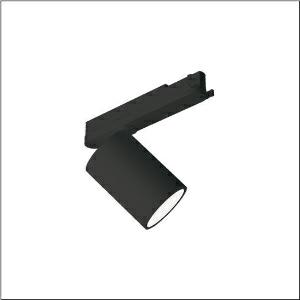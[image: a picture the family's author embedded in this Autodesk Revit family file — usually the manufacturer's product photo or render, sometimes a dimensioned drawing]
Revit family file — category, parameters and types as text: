
# Revit family: spot_31_51sf34mad4b
name_source: partatom
category: Lighting Fixtures
units: mm (PartAtom-declared; Revit-internal decimal feet)

## family parameters
Cut with Voids When Loaded = No
Host = Face
Light Source = No
Part Type = Normal
Room Calculation Point = No
Round Connector Dimension = Use Diameter
Shared = No

## types (1)
- --- (1 x LED, 5250 lm, 41.4 W, 4000K)
    Apparent Load = 41 VA
    CIE Flux Codes = 93 97 100 100 100
    Color Rendering = 90
    Color Temperature = 4000K
    Default Elevation = 1800 mm
    Description = Spot 31, directional spotlight, light control with lens, of PMMA, LED rated luminous flux: 5.040lm, light colour: 940, with 3-phase adapter, mains connection: 220..240V, AC, 50/60Hz, of aluminium, jet black (RAL 9005), length: 213mm, diameter: 90mm, protection rating (complete): IP20, insulation class (complete): insulation class I (protective earthing), certification: CE, impact resistance: IK02, permissible ambient temperature for indoor applications: -20..+40°C, packaging unit: 1 piece
    Height = 175 mm
    Lamp = 1 x LED
    Lamp Light Flux = 5250 lm
    Lamp Power = 41.4 W
    Lamp count = 1
    Length = 90 mm
    Luminous efficacy = 127 lm/W
    Manufacturer = Siteco
    ModVariant = No
    Model = 51SF34MAD4B
    Mounting Place = Ceiling
    Mounting Type = Pendant
    Number of Poles = 1
    OnlyDefault = Yes
    Power Factor = 1
    Product Name = Spot 31
    Product group = directional spotlight
    ProductGroupID = 905
    Protection Class = Protection class I
    Protection Degree = IP 20
    RLX_Detail_Level = 1
    RLX_Emergency_Light_Flux = 0 lm
    RLX_Emergency_Type = 0
    RLX_Emergency_Type_DB = No
    RlxData = <blob elided: 20881 chars, md5=4ae62658>
    Socket = socket
    Standby Power = 0 W
    System Light Flux = 5250 lm
    System Power = 41 W
    Type Comments = factory setting: luminous flux: 100 % | (ON | ON | ON | ON) | 1050 mA
    Type Image = l_1273723.jpg
    URL = http://relux.com
    VarID = @adj_078185
    Voltage = 0 V
    Weight = 0.00 kg
    Width = 0 mm  [stored 0 ft]

note: [stored X ft] marks values corroborated as IEEE doubles in the binary element streams (Revit-internal decimal feet)

## geometry (parser evidence)
native form markers: Blend x4, Sweep x11
no freeform markers — native parametric forms only
